# Revit family: Dozownik_mydla_w_plynie 1 l poziomy TOP H
name_source: partatom
category: Furniture
units: mm (PartAtom-declared; Revit-internal decimal feet)

## family parameters
Always vertical = Yes
Cut with Voids When Loaded = No
Host = Wall
Room Calculation Point = No
Shared = No

## types (1)
- N08024S
    Depth / Glebokosc = 72 mm  [stored 0.23622 ft]
    Description = Dozownik mydła w płynie 1l poziomy TOP H to naścienny podajnik wykonany ze stali nierdzewnej o matowym wykończeniu. Jest wygodny w montażu, praktyczny w obsłudze oraz nieuciążliwy w konserwacji. Świetnie sprawdza się w toaletach publicznych o wysokim natężeniu ruchu. Dzięki transparentnemu okienku w wygodny sposób można kontrolować poziom mydła w jego wnętrzu. To pojemnik do mydła, który doskonale trafia w gusta użytkowników.
    Height / Wysokosc = 122 mm  [stored 0.400262 ft]
    Manufacturer = FANECO.com
    Manufacturer code / Kod producenta = 5901764295792
    Material = Stal nierdzewna szczotkowana
    Material finish / Wykonczenie = Stal nierdzewna 304 szczotkowana,
    Product code / Kod produktu = S1000SPH
    Type Comments = Dozownik mydła w płynie 1 l poziomy TOP H
    URL = https://faneco.com
    Weight / Waga = 0.6 kg
    Width / Szerokosc = 202 mm  [stored 0.66273 ft]

note: [stored X ft] marks values corroborated as IEEE doubles in the binary element streams (Revit-internal decimal feet)

## geometry (parser evidence)
native form markers: Extrusion x2, Sweep x8
no freeform markers — native parametric forms only
